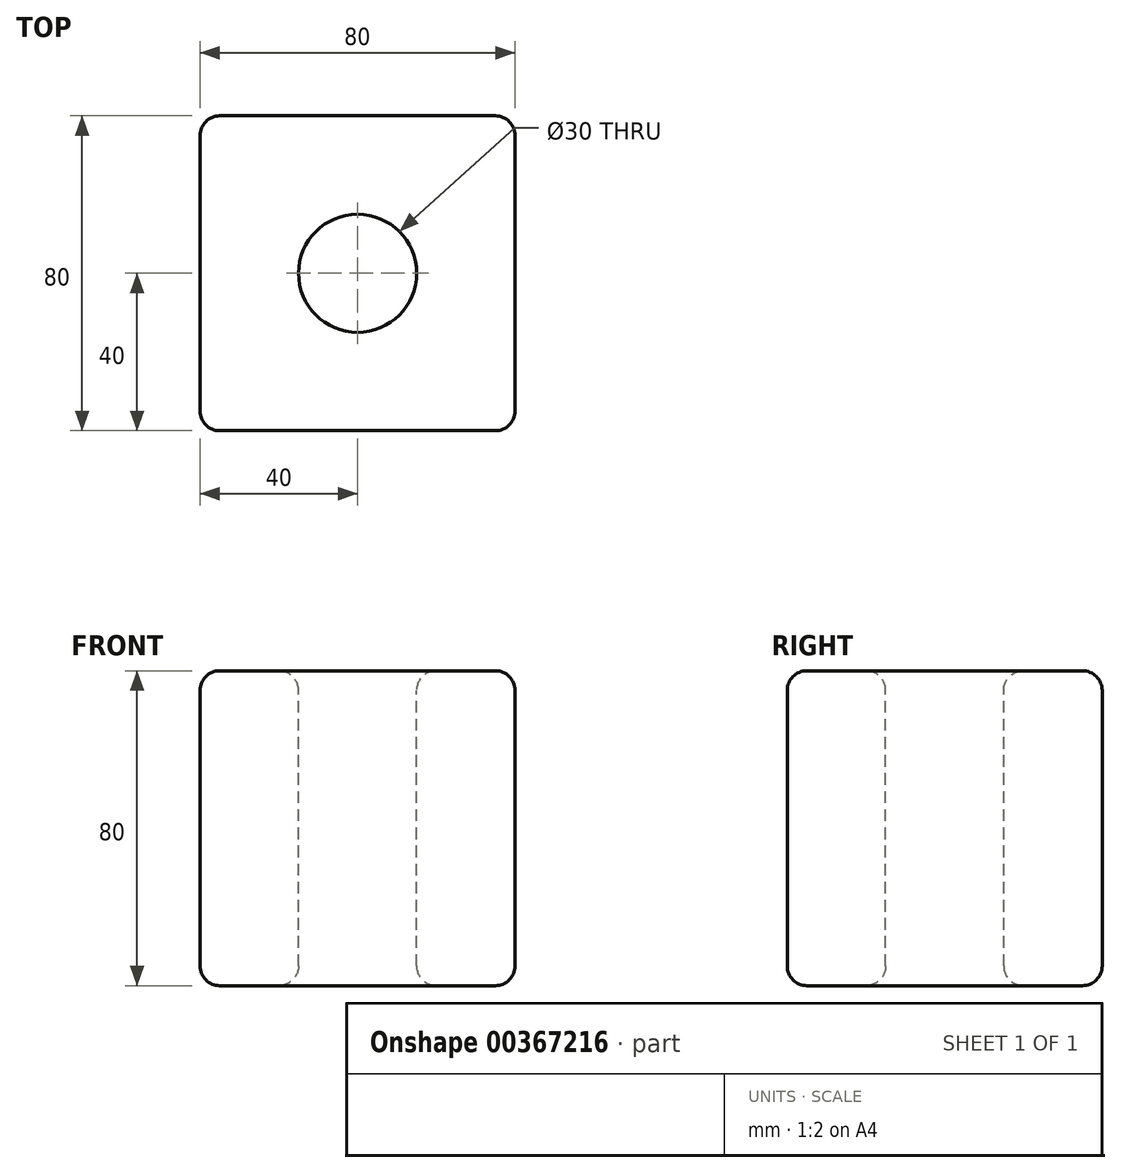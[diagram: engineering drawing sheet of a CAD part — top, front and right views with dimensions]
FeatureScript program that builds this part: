
annotation { "Feature Type Name" : "Feature", "Feature Type Description" : "" }
export const myFeature = defineFeature(function(context is Context, id is Id, definition is map)
    precondition{}
    {
        {
            var Q0;
            Q0=qCreatedBy(makeId("Top.planeOp"),FACE);
            var sketch = newSketch(context, id + "F0", { "sketchPlane" : qUnion([Q0])});
            skLineSegment(sketch, "E0.bottom", {"start": v(-40, 40) * mm, "end": v(40, 40) * mm});
            skLineSegment(sketch, "E0.top", {"start": v(-40, -40) * mm, "end": v(40, -40) * mm});
            skLineSegment(sketch, "E0.left", {"start": v(-40, 40) * mm, "end": v(-40, -40) * mm});
            skLineSegment(sketch, "E0.right", {"start": v(40, 40) * mm, "end": v(40, -40) * mm});
            skPoint(sketch, "E0.middle", {"position": v(0, 0) * mm});
            skSolve(sketch);
        }
        {
            var Q0;
            Q0=makeQuery(id+"F0.imprint","IMPRINT",FACE,{"disambiguationData":[TD([[makeQuery(id+"F0.imprint","IMPRINT",EDGE,{"derivedFrom":sQuery(id+"F0.wireOp",EDGE,"E0.bottom")}),-1.0]])]});
            extrude(context, id + "F1", {"entities" : qUnion([Q0]), "depth" : 80 * mm});
        }
        {
            var Q0;
            Q0=makeQuery(id+"F1.opExtrude","CAP_FACE",FACE,{"disambiguationData":[OSD([sQuery(id+"F0.wireOp",EDGE,"E0.bottom"),sQuery(id+"F0.wireOp",EDGE,"E0.top"),sQuery(id+"F0.wireOp",EDGE,"E0.left"),sQuery(id+"F0.wireOp",EDGE,"E0.right")])],"isStart":false});
            var sketch = newSketch(context, id + "F2", { "sketchPlane" : qUnion([Q0])});
            skCircle(sketch, "E1", {"center": v(0, 0) * mm, "radius": 15 * mm});
            skSolve(sketch);
        }
        {
            var Q0;
            Q0=makeQuery(id+"F2.imprint","IMPRINT",FACE,{"disambiguationData":[TD([[makeQuery(id+"F2.imprint","IMPRINT",EDGE,{"derivedFrom":sQuery(id+"F2.wireOp",EDGE,"E1")}),1.0]])]});
            extrude(context, id + "F3", {"entities" : qUnion([Q0]), "operationType" : NewBodyOperationType.REMOVE, "endBound" : BoundingType.THROUGH_ALL, "oppositeDirection" : true, "depth" : 25 * mm});
        }
        {
            var Q0;
            Q0=makeQuery(id+"F1.opExtrude","SWEPT_FACE",FACE,{"disambiguationData":[OSD([sQuery(id+"F0.wireOp",EDGE,"E0.right")])]});
            var Q1;
            Q1=makeQuery(id+"F1.opExtrude","CAP_FACE",FACE,{"disambiguationData":[OSD([sQuery(id+"F0.wireOp",EDGE,"E0.bottom"),sQuery(id+"F0.wireOp",EDGE,"E0.top"),sQuery(id+"F0.wireOp",EDGE,"E0.left"),sQuery(id+"F0.wireOp",EDGE,"E0.right")])],"isStart":true});
            var Q2;
            Q2=makeQuery(id+"F1.opExtrude","CAP_FACE",FACE,{"disambiguationData":[OSD([sQuery(id+"F0.wireOp",EDGE,"E0.bottom"),sQuery(id+"F0.wireOp",EDGE,"E0.top"),sQuery(id+"F0.wireOp",EDGE,"E0.left"),sQuery(id+"F0.wireOp",EDGE,"E0.right")])],"isStart":false});
            var Q3;
            Q3=makeQuery(id+"F1.opExtrude","SWEPT_FACE",FACE,{"disambiguationData":[OSD([sQuery(id+"F0.wireOp",EDGE,"E0.left")])]});
            fillet(context, id + "F4", {"entities" : qUnion([Q0, Q1, Q2, Q3]), "radius" : 5 * mm, "tangentPropagation" : true, "allowEdgeOverflow" : false});
        }
    });
